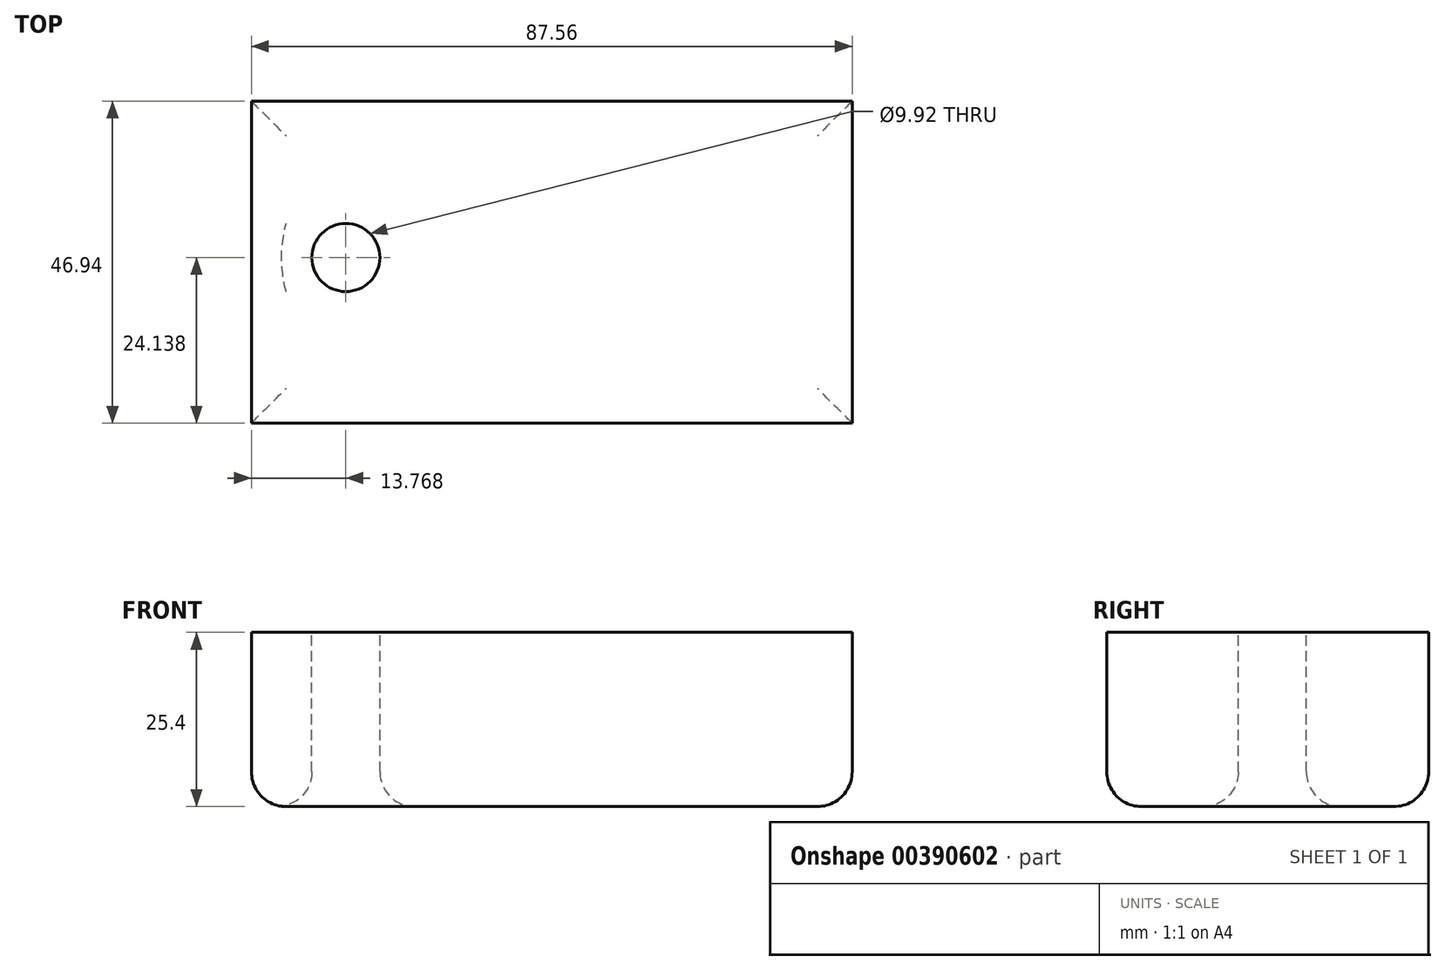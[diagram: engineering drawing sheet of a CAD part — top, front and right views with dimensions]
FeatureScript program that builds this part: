
annotation { "Feature Type Name" : "Feature", "Feature Type Description" : "" }
export const myFeature = defineFeature(function(context is Context, id is Id, definition is map)
    precondition{}
    {
        {
            var Q0;
            Q0=qCreatedBy(makeId("Top.planeOp"),FACE);
            var sketch = newSketch(context, id + "F0", { "sketchPlane" : qUnion([Q0])});
            skLineSegment(sketch, "E0.bottom", {"start": v(0, 0) * mm, "end": v(87.56, 0) * mm});
            skLineSegment(sketch, "E0.top", {"start": v(0, 46.94) * mm, "end": v(87.56, 46.94) * mm});
            skLineSegment(sketch, "E0.left", {"start": v(0, 0) * mm, "end": v(0, 46.94) * mm});
            skLineSegment(sketch, "E0.right", {"start": v(87.56, 0) * mm, "end": v(87.56, 46.94) * mm});
            skSolve(sketch);
        }
        {
            var Q0;
            Q0 = qSketchRegion(id + "F0", true);
            extrude(context, id + "F1", {"entities" : qUnion([Q0]), "depth" : 25.4 * mm});
        }
        {
            var Q0;
            Q0=makeQuery(id+"F1.opExtrude","CAP_FACE",FACE,{"disambiguationData":[OSD([sQuery(id+"F0.wireOp",EDGE,"E0.bottom"),sQuery(id+"F0.wireOp",EDGE,"E0.top"),sQuery(id+"F0.wireOp",EDGE,"E0.left"),sQuery(id+"F0.wireOp",EDGE,"E0.right")])],"isStart":false});
            var sketch = newSketch(context, id + "F2", { "sketchPlane" : qUnion([Q0])});
            skCircle(sketch, "E1", {"center": v(13.77, 24.14) * mm, "radius": 4.96 * mm});
            skSolve(sketch);
        }
        {
            var Q0;
            Q0 = qSketchRegion(id + "F2", true);
            extrude(context, id + "F3", {"entities" : qUnion([Q0]), "operationType" : NewBodyOperationType.REMOVE, "oppositeDirection" : true, "depth" : 25.4 * mm});
        }
        {
            var Q0;
            Q0=makeQuery(id+"F1.opExtrude","CAP_FACE",FACE,{"disambiguationData":[OSD([sQuery(id+"F0.wireOp",EDGE,"E0.bottom"),sQuery(id+"F0.wireOp",EDGE,"E0.top"),sQuery(id+"F0.wireOp",EDGE,"E0.left"),sQuery(id+"F0.wireOp",EDGE,"E0.right")])],"isStart":true});
            fillet(context, id + "F4", {"entities" : qUnion([Q0]), "radius" : 5.08 * mm, "tangentPropagation" : true, "allowEdgeOverflow" : false});
        }
    });
